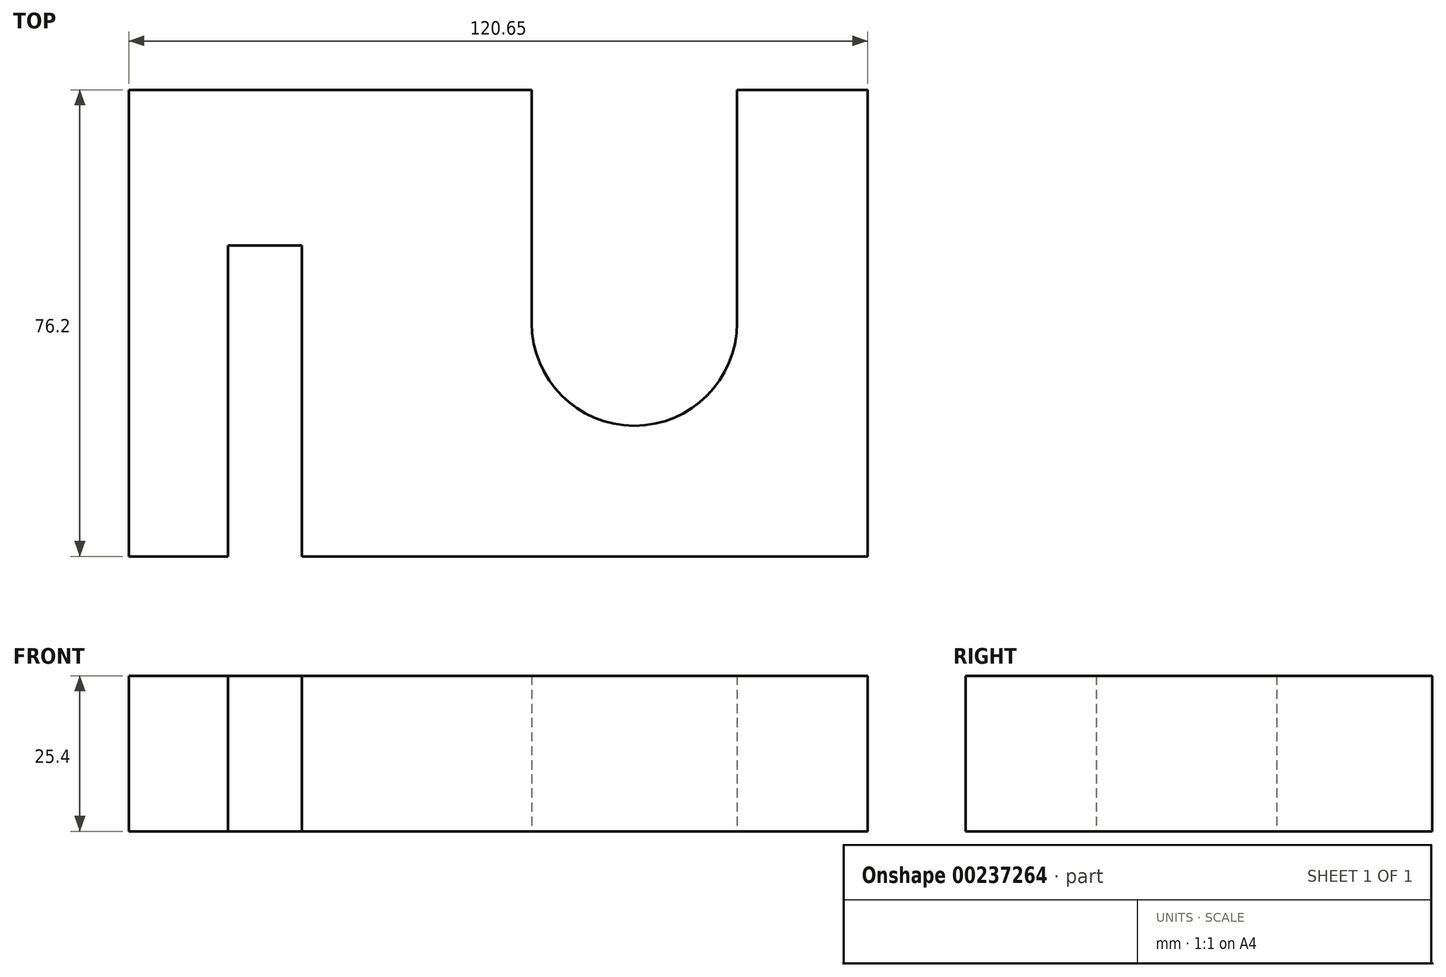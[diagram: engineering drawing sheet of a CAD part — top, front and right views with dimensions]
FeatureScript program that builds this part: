
annotation { "Feature Type Name" : "Feature", "Feature Type Description" : "" }
export const myFeature = defineFeature(function(context is Context, id is Id, definition is map)
    precondition{}
    {
        {
            var Q0;
            Q0=qCreatedBy(makeId("Top.planeOp"),FACE);
            var sketch = newSketch(context, id + "F0", { "sketchPlane" : qUnion([Q0])});
            skLineSegment(sketch, "E0.bottom", {"start": v(38.1, 38.1) * mm, "end": v(-38.1, 38.1) * mm});
            skLineSegment(sketch, "E0.top", {"start": v(38.1, -38.1) * mm, "end": v(-38.1, -38.1) * mm});
            skLineSegment(sketch, "E0.left", {"start": v(38.1, 38.1) * mm, "end": v(38.1, -38.1) * mm});
            skLineSegment(sketch, "E0.right", {"start": v(-38.1, 38.1) * mm, "end": v(-38.1, -38.1) * mm});
            skPoint(sketch, "E0.middle", {"position": v(0, 0) * mm});
            skCircle(sketch, "E1", {"center": v(0, 0) * mm, "radius": 16.76 * mm});
            skLineSegment(sketch, "E2.bottom", {"start": v(-38.1, 38.1) * mm, "end": v(-82.55, 38.1) * mm});
            skLineSegment(sketch, "E2.top", {"start": v(-38.1, -38.1) * mm, "end": v(-82.55, -38.1) * mm});
            skLineSegment(sketch, "E2.right", {"start": v(-82.55, 38.1) * mm, "end": v(-82.55, -38.1) * mm});
            skLineSegment(sketch, "E3", {"start": v(-16.76, 0) * mm, "end": v(-16.76, 38.1) * mm});
            skLineSegment(sketch, "E4", {"start": v(16.76, 0) * mm, "end": v(16.76, 38.1) * mm});
            skLineSegment(sketch, "E5", {"start": v(-60.33, -38.1) * mm, "end": v(-60.33, 38.1) * mm, "construction": true});
            skLineSegment(sketch, "E6", {"start": v(-54.3, -38.1) * mm, "end": v(-54.3, 12.7) * mm});
            skLineSegment(sketch, "E7", {"start": v(-54.3, 12.7) * mm, "end": v(-60.33, 12.7) * mm});
            skLineSegment(sketch, "E8.MirrorCS", {"start": v(-66.36, -38.1) * mm, "end": v(-66.36, 12.7) * mm});
            skLineSegment(sketch, "E9.MirrorCS", {"start": v(-66.36, 12.7) * mm, "end": v(-60.33, 12.7) * mm});
            skSolve(sketch);
        }
        {
            var Q0;
            Q0=makeQuery(id+"F0.imprint","IMPRINT",FACE,{"disambiguationData":[TD([[makeQuery(id+"F0.imprint","IMPRINT",EDGE,{"derivedFrom":sQuery(id+"F0.wireOp",EDGE,"E0.top")}),-1.0]])]});
            var Q1;
            Q1=makeQuery(id+"F0.imprint","IMPRINT",FACE,{"disambiguationData":[TD([[makeQuery(id+"F0.imprint","IMPRINT",EDGE,{"derivedFrom":sQuery(id+"F0.wireOp",EDGE,"E2.bottom")}),1.0]])]});
            extrude(context, id + "F1", {"entities" : qUnion([Q0, Q1]), "depth" : 25.4 * mm});
        }
    });
